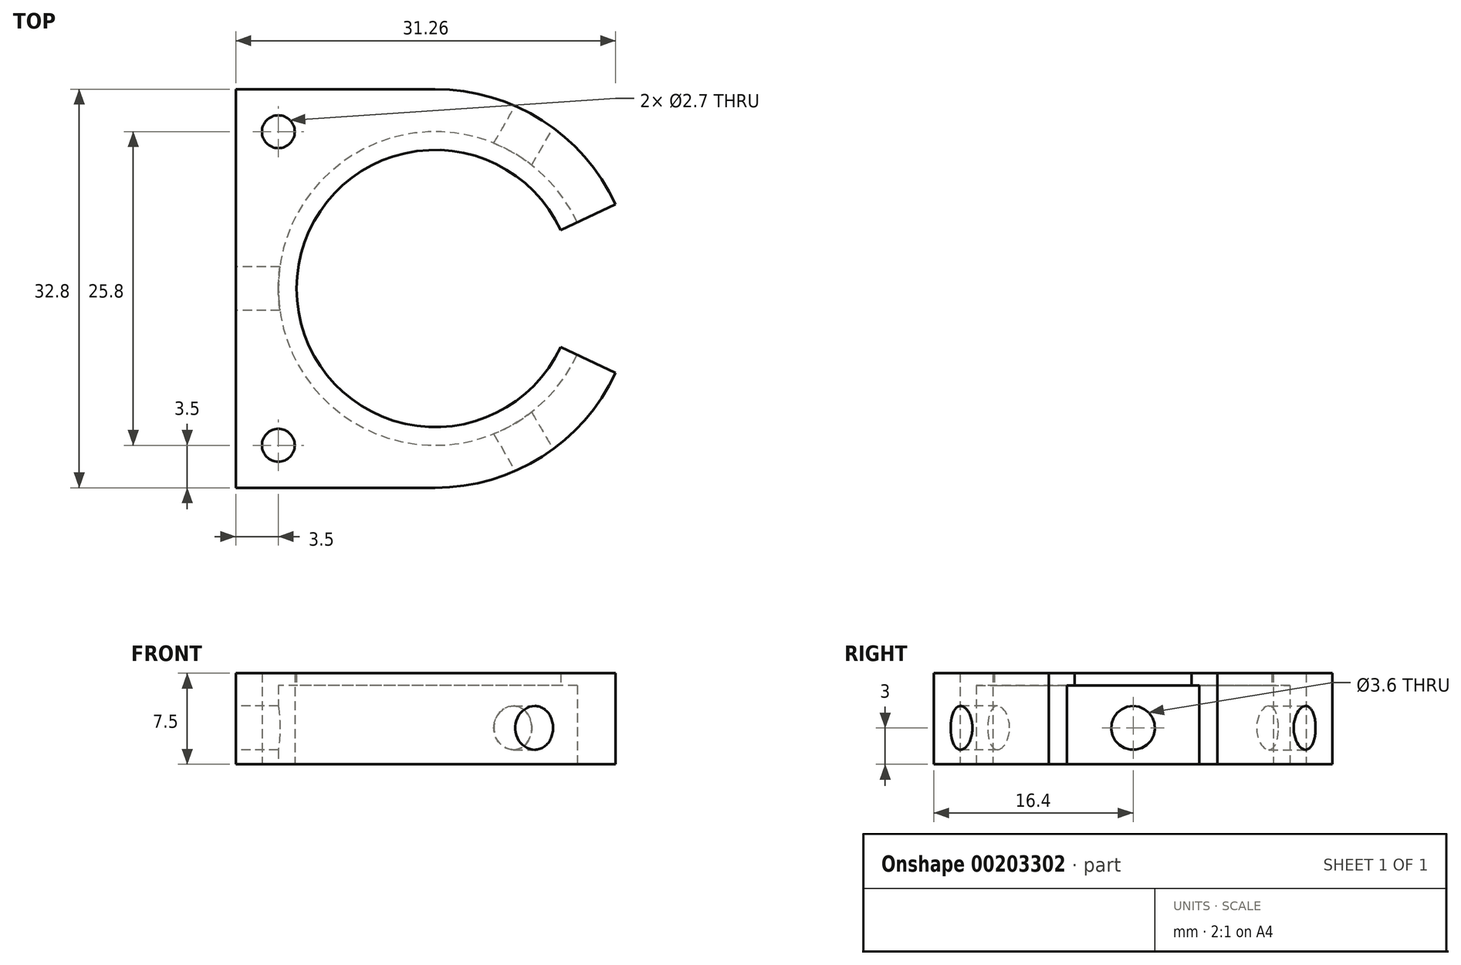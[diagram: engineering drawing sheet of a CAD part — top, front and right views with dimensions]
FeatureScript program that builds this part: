
annotation { "Feature Type Name" : "Feature", "Feature Type Description" : "" }
export const myFeature = defineFeature(function(context is Context, id is Id, definition is map)
    precondition{}
    {
        {
            var Q0;
            Q0=qCreatedBy(makeId("Top.planeOp"),FACE);
            var sketch = newSketch(context, id + "F0", { "sketchPlane" : qUnion([Q0])});
            skArc(sketch, "E0", {"start": v(10.33, 4.82) * mm, "mid": v(-11.4, 0) * mm, "end": v(10.33, -4.82) * mm});
            skArc(sketch, "E1", {"start": v(0, -16.4) * mm, "mid": v(8.81, -13.83) * mm, "end": v(14.86, -6.93) * mm});
            skLineSegment(sketch, "E2", {"start": v(0, 16.4) * mm, "end": v(-16.4, 16.4) * mm});
            skLineSegment(sketch, "E3", {"start": v(-16.4, 16.4) * mm, "end": v(-16.4, -16.4) * mm});
            skLineSegment(sketch, "E4", {"start": v(-16.4, -16.4) * mm, "end": v(0, -16.4) * mm});
            skLineSegment(sketch, "E5", {"start": v(10.33, 4.82) * mm, "end": v(14.86, 6.93) * mm});
            skLineSegment(sketch, "E6", {"start": v(10.33, -4.82) * mm, "end": v(14.86, -6.93) * mm});
            skArc(sketch, "E7.trimOffspring", {"start": v(14.86, 6.93) * mm, "mid": v(8.81, 13.83) * mm, "end": v(0, 16.4) * mm});
            skSolve(sketch);
        }
        {
            var Q0;
            Q0 = qSketchRegion(id + "F0", true);
            extrude(context, id + "F1", {"entities" : qUnion([Q0]), "depth" : 7.5 * mm});
        }
        {
            var Q0;
            Q0=makeQuery(id+"F1.opExtrude","CAP_FACE",FACE,{"disambiguationData":[OSD([sQuery(id+"F0.wireOp",EDGE,"E0"),sQuery(id+"F0.wireOp",EDGE,"E1"),sQuery(id+"F0.wireOp",EDGE,"E2"),sQuery(id+"F0.wireOp",EDGE,"E3"),sQuery(id+"F0.wireOp",EDGE,"E4"),sQuery(id+"F0.wireOp",EDGE,"E5"),sQuery(id+"F0.wireOp",EDGE,"E6"),sQuery(id+"F0.wireOp",EDGE,"E7.trimOffspring")])],"isStart":true});
            var sketch = newSketch(context, id + "F2", { "sketchPlane" : qUnion([Q0])});
            skCircle(sketch, "E8", {"center": v(0, 0) * mm, "radius": 12.9 * mm});
            skSolve(sketch);
        }
        {
            var Q0;
            Q0 = qSketchRegion(id + "F2", true);
            extrude(context, id + "F3", {"entities" : qUnion([Q0]), "operationType" : NewBodyOperationType.REMOVE, "oppositeDirection" : true, "depth" : 6.5 * mm});
        }
        {
            var Q0;
            Q0=makeQuery(id+"F1.opExtrude","CAP_FACE",FACE,{"disambiguationData":[OSD([sQuery(id+"F0.wireOp",EDGE,"E0"),sQuery(id+"F0.wireOp",EDGE,"E1"),sQuery(id+"F0.wireOp",EDGE,"E2"),sQuery(id+"F0.wireOp",EDGE,"E3"),sQuery(id+"F0.wireOp",EDGE,"E4"),sQuery(id+"F0.wireOp",EDGE,"E5"),sQuery(id+"F0.wireOp",EDGE,"E6"),sQuery(id+"F0.wireOp",EDGE,"E7.trimOffspring")])],"isStart":true});
            var sketch = newSketch(context, id + "F4", { "sketchPlane" : qUnion([Q0])});
            skLineSegment(sketch, "E9", {"start": v(0, 0) * mm, "end": v(15.76, 27.3) * mm, "construction": true});
            skLineSegment(sketch, "E10", {"start": v(0, 0) * mm, "end": v(17.19, -29.77) * mm, "construction": true});
            skPoint(sketch, "E11", {"position": v(8.2, 14.2) * mm});
            skPoint(sketch, "E12", {"position": v(8.2, -14.2) * mm});
            skSolve(sketch);
        }
        {
            var Q0;
            Q0=sQuery(id+"F4.wireOp",EDGE,"E9");
            var Q1;
            Q1=sQuery(id+"F4.wireOp",VERTEX,"E11");
            cPlane(context, id + "F5", {"entities" : qUnion([Q0, Q1]), "cplaneType" : CPlaneType.LINE_POINT, "offset" : 25 * mm, "width" : 150 * mm, "height" : 150 * mm});
        }
        {
            var Q0;
            Q0=sQuery(id+"F4.wireOp",EDGE,"E10");
            var Q1;
            Q1=sQuery(id+"F4.wireOp",VERTEX,"E12");
            cPlane(context, id + "F6", {"entities" : qUnion([Q0, Q1]), "cplaneType" : CPlaneType.LINE_POINT, "offset" : 25 * mm, "width" : 150 * mm, "height" : 150 * mm});
        }
        {
            var Q0;
            Q0=qCreatedBy(id+"F6.planeOp",FACE);
            var sketch = newSketch(context, id + "F7", { "sketchPlane" : qUnion([Q0])});
            skCircle(sketch, "E13", {"center": v(0, 3) * mm, "radius": 1.8 * mm});
            skSolve(sketch);
        }
        {
            var Q0;
            Q0 = qSketchRegion(id + "F7", true);
            extrude(context, id + "F8", {"entities" : qUnion([Q0]), "operationType" : NewBodyOperationType.REMOVE, "oppositeDirection" : true, "depth" : 10 * mm});
        }
        {
            var Q0;
            Q0=qCreatedBy(id+"F5.planeOp",FACE);
            var sketch = newSketch(context, id + "F9", { "sketchPlane" : qUnion([Q0])});
            skCircle(sketch, "E14", {"center": v(0, 3) * mm, "radius": 1.8 * mm});
            skSolve(sketch);
        }
        {
            var Q0;
            Q0 = qSketchRegion(id + "F9", true);
            extrude(context, id + "F10", {"entities" : qUnion([Q0]), "operationType" : NewBodyOperationType.REMOVE, "oppositeDirection" : true, "depth" : 10 * mm});
        }
        {
            var Q0;
            Q0=makeQuery(id+"F1.opExtrude","SWEPT_FACE",FACE,{"disambiguationData":[OSD([sQuery(id+"F0.wireOp",EDGE,"E3")])]});
            var sketch = newSketch(context, id + "F11", { "sketchPlane" : qUnion([Q0])});
            skCircle(sketch, "E15", {"center": v(0, 3) * mm, "radius": 1.8 * mm});
            skSolve(sketch);
        }
        {
            var Q0;
            Q0 = qSketchRegion(id + "F11", true);
            extrude(context, id + "F12", {"entities" : qUnion([Q0]), "operationType" : NewBodyOperationType.REMOVE, "oppositeDirection" : true, "depth" : 10 * mm});
        }
        {
            var Q0;
            Q0=makeQuery(id+"F4.imprint","IMPRINT",FACE,{"disambiguationData":[TD([[makeQuery(id+"F4.imprint","IMPRINT",EDGE,{"derivedFrom":makeQuery(id+"F1.opExtrude","CAP_EDGE",EDGE,{"disambiguationData":[OSD([sQuery(id+"F0.wireOp",EDGE,"E1")])],"isStart":true})}),-1.0]])]});
            var sketch = newSketch(context, id + "F13", { "sketchPlane" : qUnion([Q0])});
            skLineSegment(sketch, "E16", {"start": v(-12.9, -22) * mm, "end": v(-12.9, 22.14) * mm, "construction": true});
            skLineSegment(sketch, "E17", {"start": v(2.5, -12.9) * mm, "end": v(-21.6, -12.9) * mm, "construction": true});
            skLineSegment(sketch, "E18", {"start": v(1.89, 12.9) * mm, "end": v(-21, 12.9) * mm, "construction": true});
            skCircle(sketch, "E19", {"center": v(-12.9, -12.9) * mm, "radius": 1.35 * mm});
            skCircle(sketch, "E20", {"center": v(-12.9, 12.9) * mm, "radius": 1.35 * mm});
            skSolve(sketch);
        }
        {
            var Q0;
            Q0 = qSketchRegion(id + "F13", true);
            extrude(context, id + "F14", {"entities" : qUnion([Q0]), "operationType" : NewBodyOperationType.REMOVE, "endBound" : BoundingType.THROUGH_ALL, "oppositeDirection" : true, "depth" : 25 * mm});
        }
    });
